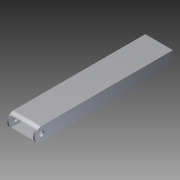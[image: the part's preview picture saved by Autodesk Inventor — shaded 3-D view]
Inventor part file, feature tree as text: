
AUTODESK INVENTOR PART (.ipt)
format: ipt  version: 2012 (Build 160160000, 160)  size: 94,720 bytes
history: native  units: in
note: dims shown in document units (in); Inventor stores cm internally (conversion verified against a paired STEP export)
features: extrude x2, sketch x2
ambient origin geometry x8: Origin, YZ Plane, XZ Plane, XY Plane, X Axis, Y Axis, Z Axis, Center Point
bodies: Solid1 (feature_tree)
feature tree (4):
  extrude  "Extrusion1"  Depth=2.0in
  extrude  "Extrusion2"  Depth=0.125in
  sketch  "Sketch1"  dims[d0=1.0in d1=2.0in]
  sketch  "Sketch2"  dims[d2=0.125in d3=0.125in d4=0.125in d5=0.125in d6=10.0in d7=0.0in d8=0.375in d9=0.5in d10=10.0in d11=0.0in]
